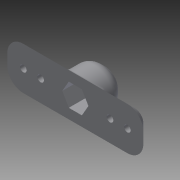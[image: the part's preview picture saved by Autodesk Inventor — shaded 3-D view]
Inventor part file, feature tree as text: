
AUTODESK INVENTOR PART (.ipt)
format: ipt  version: 2014 SP2 (Build 180246200, 246)  size: 419,840 bytes
history: native  units: mm
features: sketch x6, extrude x4, chamfer x3, fillet x3
ambient origin geometry x8: Origin, YZ Plane, XZ Plane, XY Plane, X Axis, Y Axis, Z Axis, Center Point
bodies: Solid1 (feature_tree)
feature tree (16):
  extrude  "Extrusion1"  Depth=2.5mm
  chamfer  "Chamfer1"  Distance=6.5mm
  extrude  "Extrusion2"  Depth=13.0mm
  extrude  "Extrusion3"  Depth=16.0mm
  chamfer  "Chamfer2"  Distance=8.0mm
  sketch  "Sketch4"  dims[d4=13.0mm]
  extrude  "Extrusion4"  Depth=6.0mm
  chamfer  "Chamfer3"  Distance=6.0mm
  sketch  "Sketch6"  dims[d6=2.5mm d7=6.5mm d8=13.0mm d9=16.0mm d10=8.0mm d11=6.0mm d12=6.0mm d13=6.0mm d14=8.0mm d15=14.0mm d16=6.0mm d17=3.0mm d18=0.0mm d19=3.0mm d20=2.0mm d21=45.0deg d22=10.0mm d23=8.0mm d24=0.0mm d25=8.5mm d26=7.0mm d27=0.0mm d28=4.0mm d29=2.0mm d30=45.0deg d31=15.0mm d32=11.0mm d33=0.0mm d34=2.5mm d35=2.0mm d36=45.0deg d37=4.0mm d38=2.0mm d39=1.0mm]
  fillet  "Fillet1"  Radius=6.0mm
  fillet  "Fillet2"  Radius=8.0mm
  fillet  "Fillet3"  Radius=14.0mm
  sketch  "Sketch1"  dims[d0=2.5mm d1=2.5mm]
  sketch  "Sketch2"  dims[d2=6.5mm]
  sketch  "Sketch3"  dims[d3=110.0mm]
  sketch  "Sketch5"  dims[d5=2.5mm]
